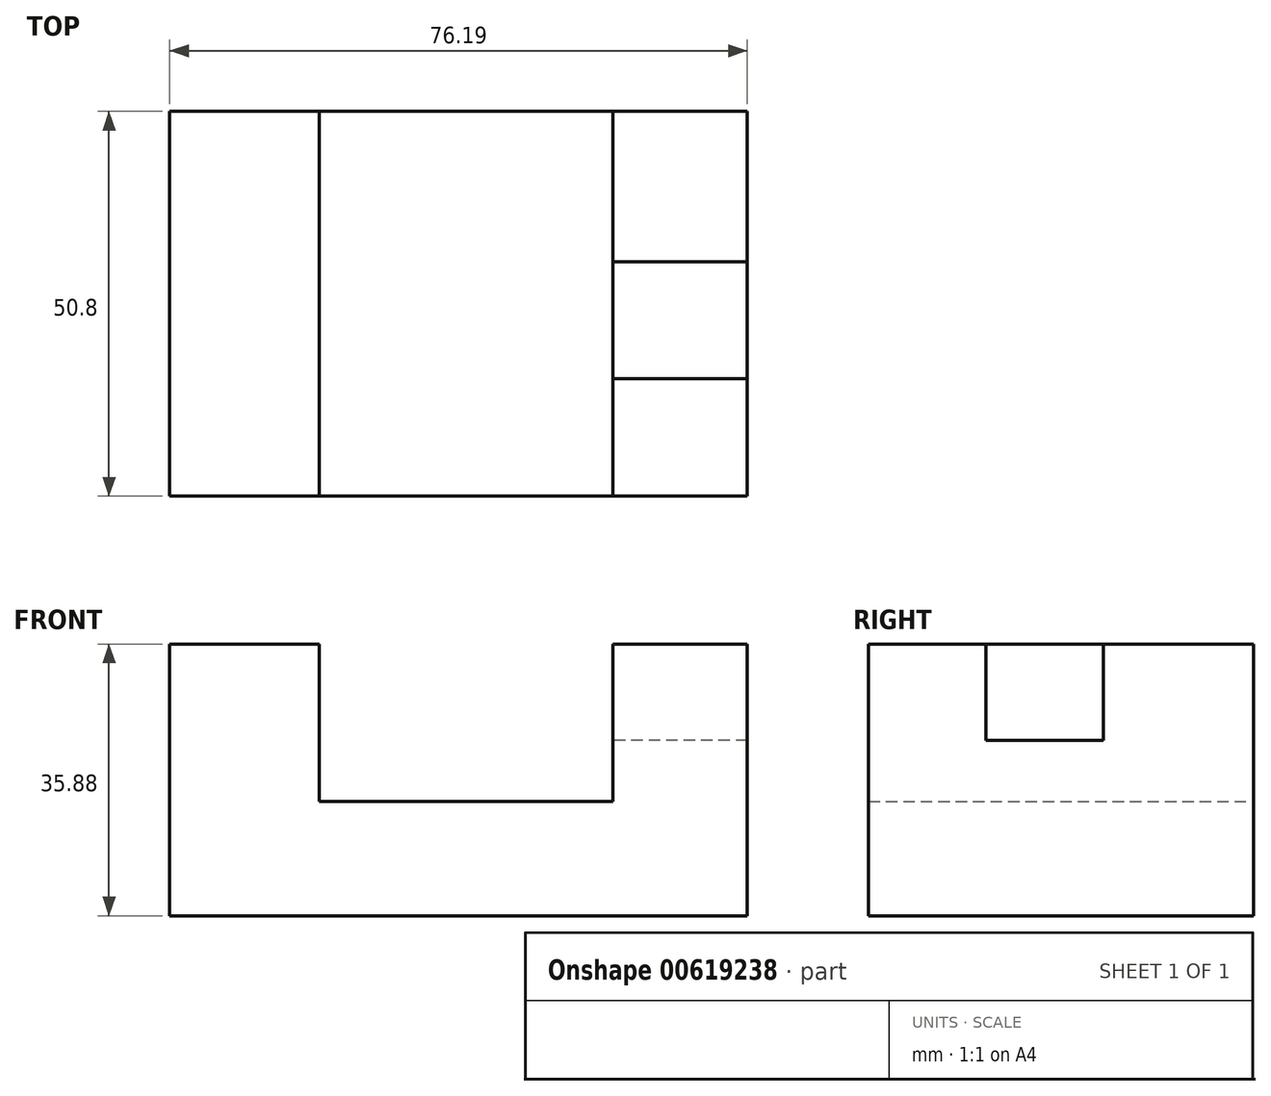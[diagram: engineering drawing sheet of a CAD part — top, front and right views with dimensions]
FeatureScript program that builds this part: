
annotation { "Feature Type Name" : "Feature", "Feature Type Description" : "" }
export const myFeature = defineFeature(function(context is Context, id is Id, definition is map)
    precondition{}
    {
        {
            var Q0;
            Q0=qCreatedBy(makeId("Front.planeOp"),FACE);
            var sketch = newSketch(context, id + "F0", { "sketchPlane" : qUnion([Q0])});
            skLineSegment(sketch, "E0.bottom", {"start": v(0, 0) * mm, "end": v(76.2, 0) * mm});
            skLineSegment(sketch, "E0.top", {"start": v(0, 35.88) * mm, "end": v(19.7, 35.88) * mm});
            skLineSegment(sketch, "E0.left", {"start": v(0, 0) * mm, "end": v(0, 35.88) * mm});
            skLineSegment(sketch, "E0.right", {"start": v(76.2, 0) * mm, "end": v(76.2, 35.88) * mm});
            skLineSegment(sketch, "E1", {"start": v(19.7, 35.88) * mm, "end": v(19.7, 15.12) * mm});
            skLineSegment(sketch, "E2", {"start": v(19.7, 15.12) * mm, "end": v(58.48, 15.12) * mm});
            skLineSegment(sketch, "E3", {"start": v(58.48, 14.81) * mm, "end": v(58.48, 35.88) * mm});
            skLineSegment(sketch, "E4.trimOffspring", {"start": v(58.48, 35.88) * mm, "end": v(76.2, 35.88) * mm});
            skSolve(sketch);
        }
        {
            var Q0;
            Q0=makeQuery(id+"F0.imprint","IMPRINT",FACE,{"disambiguationData":[TD([[makeQuery(id+"F0.imprint","IMPRINT",EDGE,{"derivedFrom":sQuery(id+"F0.wireOp",EDGE,"E0.bottom")}),1.0]])]});
            extrude(context, id + "F1", {"entities" : qUnion([Q0]), "depth" : 25.4 * mm, "offsetDistance" : 25.4 * mm});
        }
        {
            var Q0;
            Q0=makeQuery(id+"F1.opExtrude","CAP_FACE",FACE,{"disambiguationData":[OSD([sQuery(id+"F0.wireOp",EDGE,"E0.bottom"),sQuery(id+"F0.wireOp",EDGE,"E0.top"),sQuery(id+"F0.wireOp",EDGE,"E0.left"),sQuery(id+"F0.wireOp",EDGE,"E0.right"),sQuery(id+"F0.wireOp",EDGE,"E1"),sQuery(id+"F0.wireOp",EDGE,"E2"),sQuery(id+"F0.wireOp",EDGE,"E3"),sQuery(id+"F0.wireOp",EDGE,"E4.trimOffspring")])],"isStart":false});
            extrude(context, id + "F2", {"entities" : qUnion([Q0]), "operationType" : NewBodyOperationType.ADD, "depth" : 25.4 * mm, "offsetDistance" : 25.4 * mm});
        }
        {
            var Q0;
            {var subQ0=sQuery(id+"F0.wireOp",EDGE,"E4.trimOffspring");Q0=makeQuery(id+"F2.boolean.opBoolean","MERGE",FACE,{"derivedFrom":[makeQuery(id+"F1.opExtrude","SWEPT_FACE",FACE,{"disambiguationData":[OSD([subQ0])]}),makeQuery(id+"F2.opExtrude","SWEPT_FACE",FACE,{"disambiguationData":[OSD([subQ0])]})]});}
            var sketch = newSketch(context, id + "F3", { "sketchPlane" : qUnion([Q0])});
            skLineSegment(sketch, "E5", {"start": v(76.2, -35.3) * mm, "end": v(58.48, -35.3) * mm});
            skLineSegment(sketch, "E6", {"start": v(76.2, -19.85) * mm, "end": v(58.48, -19.85) * mm});
            skLineSegment(sketch, "E7", {"start": v(76.2, -19.85) * mm, "end": v(76.2, -35.3) * mm});
            skLineSegment(sketch, "E8", {"start": v(58.48, -19.85) * mm, "end": v(58.48, -35.3) * mm});
            skSolve(sketch);
        }
        {
            var Q0;
            Q0=makeQuery(id+"F3.imprint","IMPRINT",FACE,{"disambiguationData":[TD([[makeQuery(id+"F3.imprint","IMPRINT",EDGE,{"derivedFrom":sQuery(id+"F3.wireOp",EDGE,"E5")}),-1.0]])]});
            extrude(context, id + "F4", {"entities" : qUnion([Q0]), "operationType" : NewBodyOperationType.REMOVE, "endBound" : BoundingType.SYMMETRIC, "oppositeDirection" : true, "depth" : 25.4 * mm, "offsetDistance" : 25.4 * mm});
        }
    });
